# Revit family: IlluminatedMirrorCabinet-120cm-Vitra-EliteSeries-56789+56790+56791+56793+56796+58226
name_source: partatom
category: Furniture Systems
revit_build: Autodesk Revit 2017 (Build: 20160225_1515(x64)
units: mm (PartAtom-declared; Revit-internal decimal feet)

## family parameters
Cut with Voids When Loaded = No
Host = Face
OmniClass Number = 23.40.00.00
OmniClass Title = Equipment and Furnishings
Part Type = Normal
Room Calculation Point = No
Round Connector Dimension = Use Diameter
Shared = Yes

## types (6) — shared parameters
BIMobject category = Storage
Construction Type = Wall Mounted
Default Elevation = 1255 mm  [stored 4.11745 ft]
Depth(mm) = 150 mm
Description = Elite Illuminated Mirror Cabinet
Design country = Turkey
Height(mm) = 700 mm  [stored 2.29659 ft]
IFC Classification = Furnishing Element
Installation instructions = https://cdn.vitra.com.tr
Lighting Type = Sandblasted Led Lighting
Manufacturer = Vitra
Manufacturer name = Vitra
Masterformat 2014 Code = 41 53 13
Masterformat 2014 Description = Storage Cabinets
NBS Referans Code = 35-75-08
NBS Referans Description = Bathroom Cabinets
Nominal height = 0.000
Nominal width = 0.000
OmniClass Code = 23-25 53 11 13 11
OmniClass Description = Medicine Cabinets
Primary Material = Mirror
Product certification = https://vitraglobal.com
Product data url = https://www.vitraglobal.com
Product family = Elite
Product group = Bathroom Furniture
Technical description = https://www.vitraglobal.com
Thrid Material = Light
UNSPSC Code = 30161801
UNSPSC Description = Bathroom cabinets
URL = https://vitraglobal.com
Uniclass 1.4 Code = L72141
Uniclass 1.4 Description = Cabinets
Uniclass 2.0 Code = PR-35-75-08
Uniclass 2.0 Description = Bathroom Cabinets
Uniclass 2015 Code = Pr_40_30_78_03
Uniclass 2015 Name = Bathroom cabinets
Uniformat II Code = E20
Uniformat II Description = Furnishings
Voltage = 220V
Warranty Period (Year) = 2
Weight Net (kg) = 43
Width(mm) = 1200 mm
Youtube = https://www.youtube.com

## per-type parameters (varying)
| type | Article No. (default) | Color | Model | Product SKU | Secondary Material |
| MirrorCabinet(Illuminated)-120cm-GoldenCherry-Vitra-EliteSeries_56789 | 56789 | Golden Cherry | 56789 | 56789 | Vitra-Altın Kiraz |
| MirrorCabinet(Illuminated)-120cm-HighGlossWhite-Vitra-EliteSeries_56790 | 56790 | High Gloss White | 56790 | 56790 | White |
| MirrorCabinet(Illuminated)-120cm-Oak-Vitra-EliteSeries_56791 | 56791 | Oak | 56791 | 56791 | Vitra-HareliSiyahMeşe |
| MirrorCabinet(Illuminated)-120cm-DarkOak-Vitra-EliteSeries_56793 | 56793 | DarkOak | 56793 | 56793 | Vitra-MetalikCeviz |
| MirrorCabinet(Illuminated)-120cm-Valnut-Vitra-EliteSeries_56796 | 56796 | Valnut | 56796 | 56796 | Vitra-AmericanValnut |
| MirrorCabinet(Illuminated)-120cm-MatteWhite-Vitra-EliteSeries_58226 | 58226 | Matte White | 58226 | 58226 | Vitra-MattWhite |

note: [stored X ft] marks values corroborated as IEEE doubles in the binary element streams (Revit-internal decimal feet)

## geometry (parser evidence)
native form markers: Sweep x3
no freeform markers — native parametric forms only
